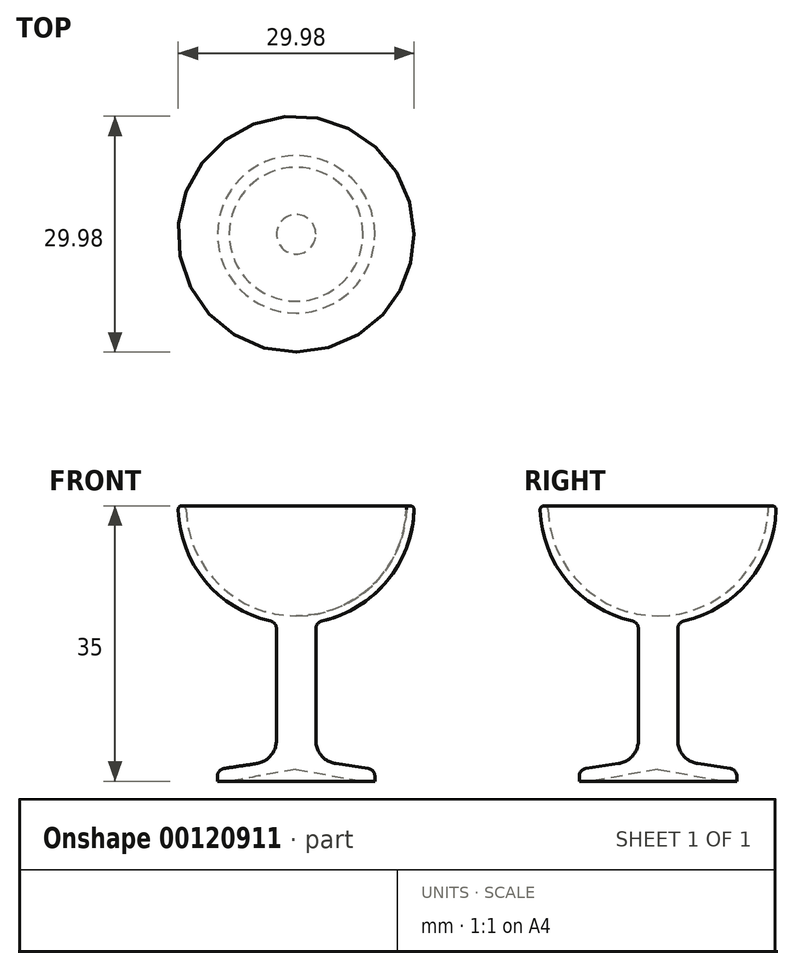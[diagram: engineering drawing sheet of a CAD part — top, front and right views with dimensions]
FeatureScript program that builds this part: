
annotation { "Feature Type Name" : "Feature", "Feature Type Description" : "" }
export const myFeature = defineFeature(function(context is Context, id is Id, definition is map)
    precondition{}
    {
        {
            var Q0;
            Q0=qCreatedBy(makeId("Front.planeOp"),FACE);
            var sketch = newSketch(context, id + "F0", { "sketchPlane" : qUnion([Q0])});
            skLineSegment(sketch, "E0", {"start": v(0, -4.47) * mm, "end": v(0, 42.63) * mm, "construction": true});
            skLineSegment(sketch, "E1", {"start": v(0, 1.5) * mm, "end": v(8.5, 0) * mm});
            skLineSegment(sketch, "E2", {"start": v(8.5, 0) * mm, "end": v(10, 0) * mm});
            skLineSegment(sketch, "E3", {"start": v(10, 0) * mm, "end": v(10, 0.64) * mm});
            skLineSegment(sketch, "E4", {"start": v(2.5, 5.2) * mm, "end": v(2.5, 19.39) * mm});
            skArc(sketch, "E5", {"start": v(3.28, 20.36) * mm, "mid": v(11.7, 25.63) * mm, "end": v(15, 35) * mm});
            skLineSegment(sketch, "E6", {"start": v(0, 35) * mm, "end": v(28, 35) * mm, "construction": true});
            skLineSegment(sketch, "E7", {"start": v(5.06, 2.24) * mm, "end": v(9.15, 1.63) * mm});
            skPoint(sketch, "E8.visualSharp", {"position": v(2.5, 2.62) * mm});
            skArc(sketch, "E8.filletArc", {"start": v(2.5, 5.2) * mm, "mid": v(3.23, 3.25) * mm, "end": v(5.06, 2.24) * mm});
            skPoint(sketch, "E9.visualSharp", {"position": v(10, 1.5) * mm});
            skArc(sketch, "E9.filletArc", {"start": v(10, 0.64) * mm, "mid": v(9.76, 1.3) * mm, "end": v(9.15, 1.63) * mm});
            skPoint(sketch, "E10.visualSharp", {"position": v(2.5, 20.2) * mm});
            skArc(sketch, "E10.filletArc", {"start": v(3.28, 20.36) * mm, "mid": v(2.72, 20.01) * mm, "end": v(2.5, 19.39) * mm});
            skArc(sketch, "E11", {"start": v(0, 21) * mm, "mid": v(9.9, 25.1) * mm, "end": v(14, 35) * mm});
            skLineSegment(sketch, "E12", {"start": v(14, 35) * mm, "end": v(15, 35) * mm});
            skLineSegment(sketch, "E13", {"start": v(0, 21) * mm, "end": v(0, 1.5) * mm});
            skSolve(sketch);
        }
        {
            var Q0;
            Q0 = qSketchRegion(id + "F0", true);
            var Q1;
            Q1=sQuery(id+"F0.wireOp",EDGE,"E0");
            revolve(context, id + "F1", {"surfaceOperationType" : NewSurfaceOperationType.NEW, "entities" : qUnion([Q0]), "axis" : qUnion([Q1]), "revolveType" : RevolveType.FULL});
        }
        {
            var Q0;
            Q0=makeQuery(id+"F1.opRevolve","SWEPT_EDGE",EDGE,{"disambiguationData":[OSD([sQuery(id+"F0.wireOp",EDGE,"E11"),sQuery(id+"F0.wireOp",EDGE,"E12")])]});
            var Q1;
            Q1=makeQuery(id+"F1.opRevolve","SWEPT_EDGE",EDGE,{"disambiguationData":[OSD([sQuery(id+"F0.wireOp",EDGE,"E5"),sQuery(id+"F0.wireOp",EDGE,"E12")])]});
            fillet(context, id + "F2", {"entities" : qUnion([Q0, Q1]), "radius" : 0.5 * mm, "tangentPropagation" : true, "allowEdgeOverflow" : false});
        }
    });
